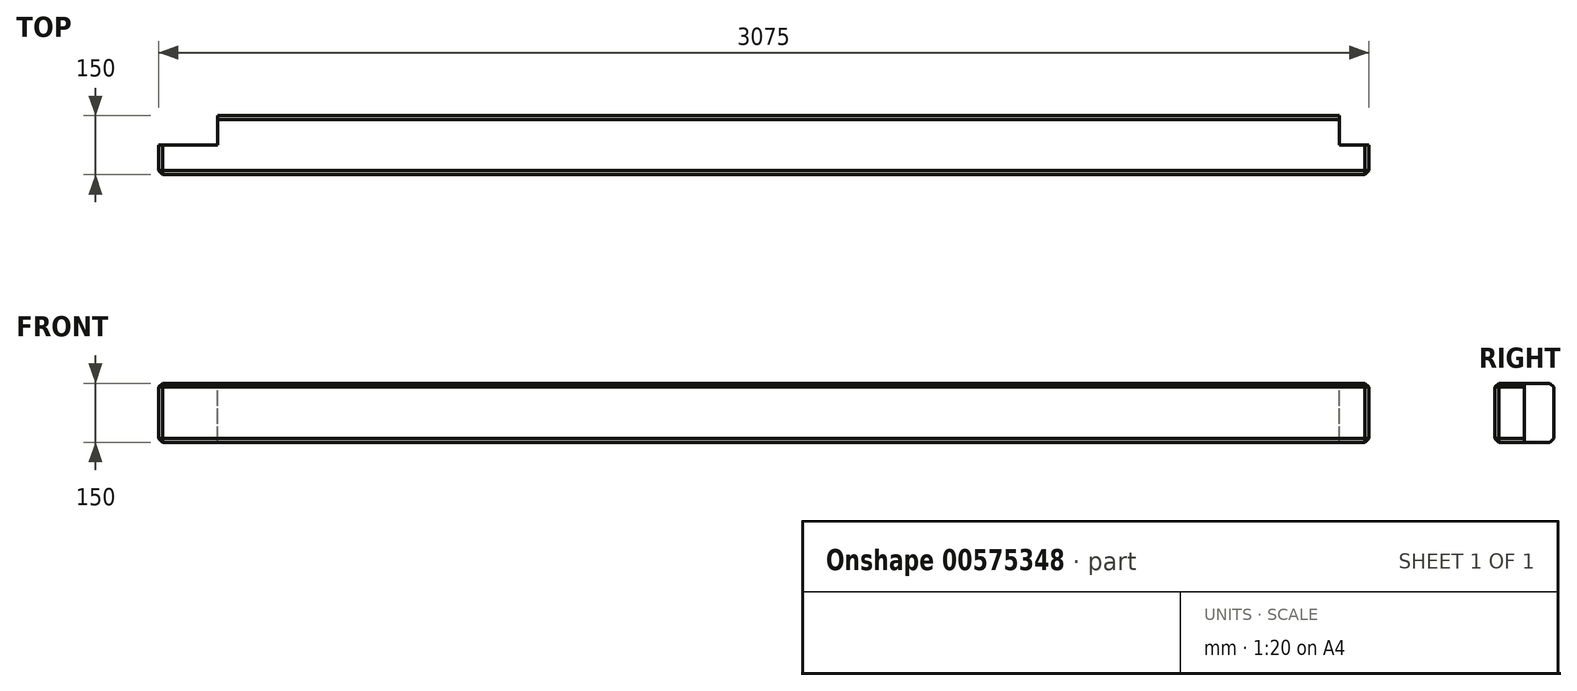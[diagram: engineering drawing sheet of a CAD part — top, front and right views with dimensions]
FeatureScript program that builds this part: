
annotation { "Feature Type Name" : "Feature", "Feature Type Description" : "" }
export const myFeature = defineFeature(function(context is Context, id is Id, definition is map)
    precondition{}
    {
        {
            var Q0;
            Q0=qCreatedBy(makeId("Top.planeOp"),FACE);
            var sketch = newSketch(context, id + "F0", { "sketchPlane" : qUnion([Q0])});
            skLineSegment(sketch, "E0.bottom", {"start": v(-1537.5, 75) * mm, "end": v(1537.5, 75) * mm});
            skLineSegment(sketch, "E0.top", {"start": v(-1537.5, -75) * mm, "end": v(1537.5, -75) * mm});
            skLineSegment(sketch, "E0.left", {"start": v(-1537.5, 75) * mm, "end": v(-1537.5, -75) * mm});
            skLineSegment(sketch, "E0.right", {"start": v(1537.5, 75) * mm, "end": v(1537.5, -75) * mm});
            skPoint(sketch, "E0.middle", {"position": v(0, 0) * mm});
            skSolve(sketch);
        }
        {
            var Q0;
            Q0=makeQuery(id+"F0.imprint","IMPRINT",FACE,{"disambiguationData":[TD([[makeQuery(id+"F0.imprint","IMPRINT",EDGE,{"derivedFrom":sQuery(id+"F0.wireOp",EDGE,"E0.bottom")}),-1.0]])]});
            extrude(context, id + "F1", {"entities" : qUnion([Q0]), "depth" : 150 * mm});
        }
        {
            var Q0;
            Q0=makeQuery(id+"F1.opExtrude","CAP_FACE",FACE,{"disambiguationData":[OSD([sQuery(id+"F0.wireOp",EDGE,"E0.bottom"),sQuery(id+"F0.wireOp",EDGE,"E0.top"),sQuery(id+"F0.wireOp",EDGE,"E0.left"),sQuery(id+"F0.wireOp",EDGE,"E0.right")])],"isStart":false});
            var Q1;
            Q1=makeQuery(id+"F1.opExtrude","SWEPT_FACE",FACE,{"disambiguationData":[OSD([sQuery(id+"F0.wireOp",EDGE,"E0.top")])]});
            var Q2;
            Q2=makeQuery(id+"F1.opExtrude","SWEPT_EDGE",EDGE,{"disambiguationData":[OSD([sQuery(id+"F0.wireOp",EDGE,"E0.bottom"),sQuery(id+"F0.wireOp",EDGE,"E0.left")])]});
            var Q3;
            Q3=makeQuery(id+"F1.opExtrude","CAP_FACE",FACE,{"disambiguationData":[OSD([sQuery(id+"F0.wireOp",EDGE,"E0.bottom"),sQuery(id+"F0.wireOp",EDGE,"E0.top"),sQuery(id+"F0.wireOp",EDGE,"E0.left"),sQuery(id+"F0.wireOp",EDGE,"E0.right")])],"isStart":true});
            var Q4;
            Q4=makeQuery(id+"F1.opExtrude","SWEPT_FACE",FACE,{"disambiguationData":[OSD([sQuery(id+"F0.wireOp",EDGE,"E0.bottom")])]});
            chamfer(context, id + "F2", {"entities" : qUnion([Q0, Q1, Q2, Q3, Q4]), "width" : 10 * mm, "tangentPropagation" : true});
        }
        {
            var Q0;
            Q0=makeQuery(id+"F1.opExtrude","CAP_FACE",FACE,{"disambiguationData":[OSD([sQuery(id+"F0.wireOp",EDGE,"E0.bottom"),sQuery(id+"F0.wireOp",EDGE,"E0.top"),sQuery(id+"F0.wireOp",EDGE,"E0.left"),sQuery(id+"F0.wireOp",EDGE,"E0.right")])],"isStart":false});
            var sketch = newSketch(context, id + "F3", { "sketchPlane" : qUnion([Q0])});
            skLineSegment(sketch, "E1.bottom", {"start": v(1537.5, 75) * mm, "end": v(1462.5, 75) * mm});
            skLineSegment(sketch, "E1.top", {"start": v(1537.5, 0) * mm, "end": v(1462.5, 0) * mm});
            skLineSegment(sketch, "E1.left", {"start": v(1537.5, 75) * mm, "end": v(1537.5, 0) * mm});
            skLineSegment(sketch, "E1.right", {"start": v(1462.5, 75) * mm, "end": v(1462.5, 0) * mm});
            skSolve(sketch);
        }
        {
            var Q0;
            {var subQ8=sQuery(id+"F3.wireOp",EDGE,"E1.bottom");Q0=makeQuery(id+"F3.imprint","IMPRINT",FACE,{"disambiguationData":[TD([[makeQuery(id+"F3.imprint","IMPRINT",EDGE,{"derivedFrom":subQ8}),1.0]])]});}
            var Q1;
            {var subQ0=sQuery(id+"F3.wireOp",EDGE,"E1.right");var subQ1=sQuery(id+"F3.wireOp",EDGE,"E1.top");var subQ2=makeQuery(id+"F3.imprint","INTERSECT",VERTEX,{"derivedFrom":[subQ1,subQ0]});Q1=makeQuery(id+"F3.imprint","IMPRINT",FACE,{"disambiguationData":[TD([[makeQuery(id+"F3.imprint","IMPRINT",EDGE,{"disambiguationData":[TD([[subQ2,1.0]])],"derivedFrom":subQ1}),-1.0]])]});}
            extrude(context, id + "F4", {"entities" : qUnion([Q0, Q1]), "operationType" : NewBodyOperationType.REMOVE, "endBound" : BoundingType.THROUGH_ALL, "oppositeDirection" : true, "depth" : 25 * mm});
        }
        {
            var Q0;
            Q0=makeQuery(id+"F1.opExtrude","CAP_FACE",FACE,{"disambiguationData":[OSD([sQuery(id+"F0.wireOp",EDGE,"E0.bottom"),sQuery(id+"F0.wireOp",EDGE,"E0.top"),sQuery(id+"F0.wireOp",EDGE,"E0.left"),sQuery(id+"F0.wireOp",EDGE,"E0.right")])],"isStart":false});
            var sketch = newSketch(context, id + "F5", { "sketchPlane" : qUnion([Q0])});
            skPoint(sketch, "E2", {"position": v(-1387.5, 75) * mm});
            skLineSegment(sketch, "E3.bottom", {"start": v(-1387.5, 75) * mm, "end": v(-1537.5, 75) * mm});
            skLineSegment(sketch, "E3.top", {"start": v(-1387.5, 0) * mm, "end": v(-1537.5, 0) * mm});
            skLineSegment(sketch, "E3.left", {"start": v(-1387.5, 75) * mm, "end": v(-1387.5, 0) * mm});
            skLineSegment(sketch, "E3.right", {"start": v(-1537.5, 75) * mm, "end": v(-1537.5, 0) * mm});
            skSolve(sketch);
        }
        {
            var Q0;
            {var subQ2=sQuery(id+"F5.wireOp",EDGE,"E3.bottom");Q0=makeQuery(id+"F5.imprint","IMPRINT",FACE,{"disambiguationData":[TD([[makeQuery(id+"F5.imprint","IMPRINT",EDGE,{"derivedFrom":subQ2}),1.0]])]});}
            var Q1;
            {var subQ0=sQuery(id+"F5.wireOp",EDGE,"E3.left");var subQ1=sQuery(id+"F5.wireOp",EDGE,"E3.top");var subQ2=makeQuery(id+"F5.imprint","INTERSECT",VERTEX,{"derivedFrom":[subQ1,subQ0]});Q1=makeQuery(id+"F5.imprint","IMPRINT",FACE,{"disambiguationData":[TD([[makeQuery(id+"F5.imprint","IMPRINT",EDGE,{"disambiguationData":[TD([[subQ2,-1.0]])],"derivedFrom":subQ1}),-1.0]])]});}
            extrude(context, id + "F6", {"entities" : qUnion([Q0, Q1]), "operationType" : NewBodyOperationType.REMOVE, "endBound" : BoundingType.THROUGH_ALL, "oppositeDirection" : true, "depth" : 25 * mm});
        }
    });
